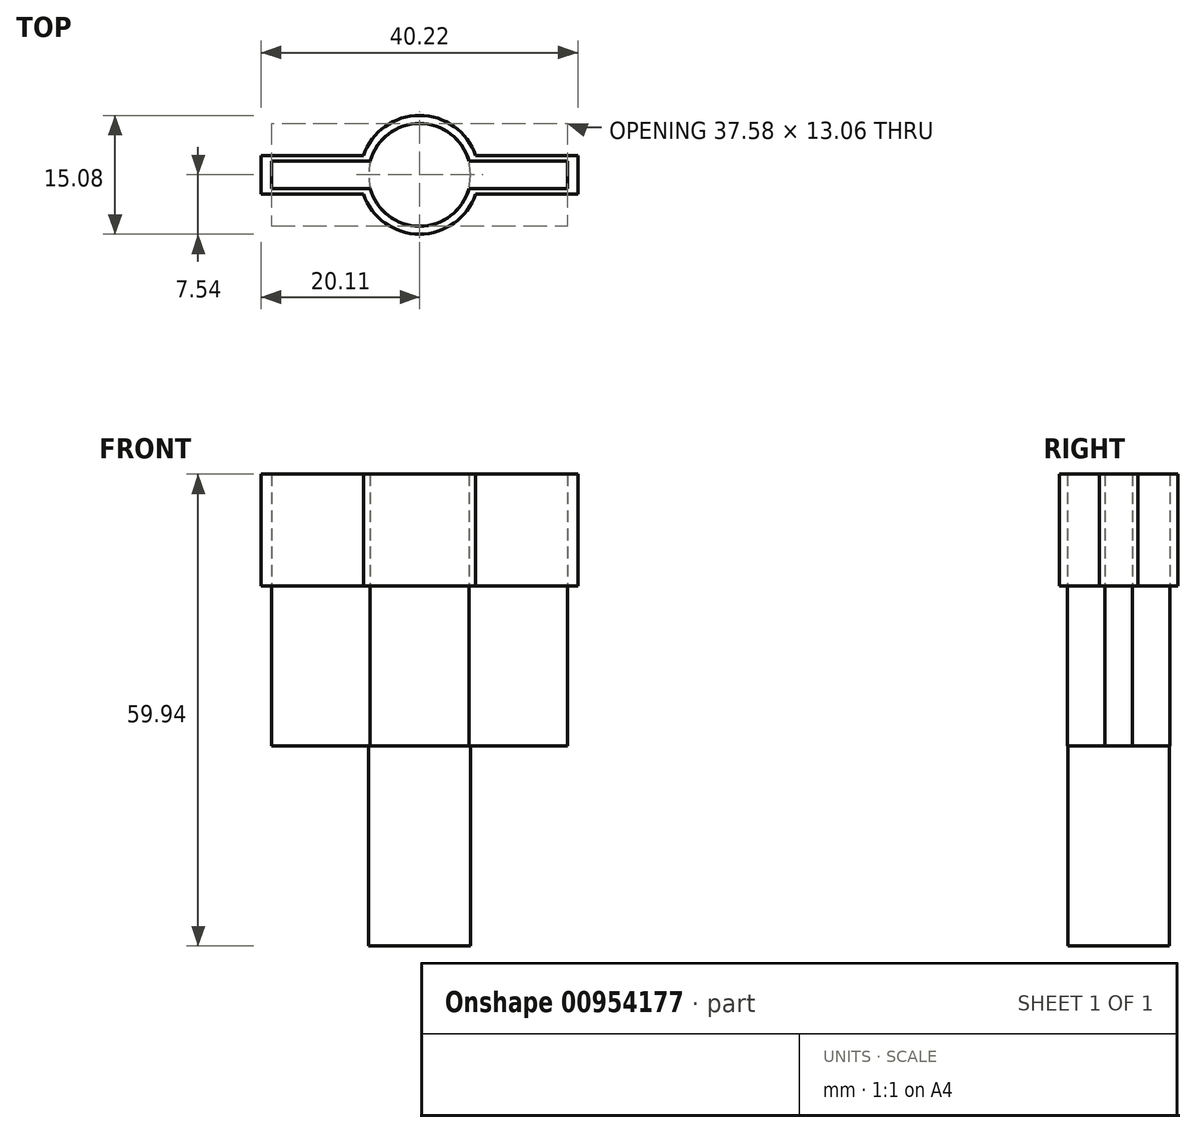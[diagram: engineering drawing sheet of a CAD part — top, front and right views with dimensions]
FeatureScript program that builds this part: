
annotation { "Feature Type Name" : "Feature", "Feature Type Description" : "" }
export const myFeature = defineFeature(function(context is Context, id is Id, definition is map)
    precondition{}
    {
        {
            var Q0;
            Q0=qCreatedBy(makeId("Top.planeOp"),FACE);
            var sketch = newSketch(context, id + "F0", { "sketchPlane" : qUnion([Q0])});
            skCircle(sketch, "E0", {"center": v(0, 0) * mm, "radius": 6.47 * mm});
            skSolve(sketch);
        }
        {
            var Q0;
            Q0=makeQuery(id+"F0.imprint","IMPRINT",FACE,{"disambiguationData":[TD([[makeQuery(id+"F0.imprint","IMPRINT",EDGE,{"derivedFrom":sQuery(id+"F0.wireOp",EDGE,"E0")}),1.0]])]});
            extrude(context, id + "F1", {"entities" : qUnion([Q0]), "depth" : 25.4 * mm, "offsetDistance" : 25.4 * mm});
        }
        {
            var Q0;
            Q0=makeQuery(id+"F1.opExtrude","CAP_FACE",FACE,{"disambiguationData":[OSD([sQuery(id+"F0.wireOp",EDGE,"E0")])],"isStart":false});
            var sketch = newSketch(context, id + "F2", { "sketchPlane" : qUnion([Q0])});
            skLineSegment(sketch, "E1.bottom", {"start": v(18.8, -1.74) * mm, "end": v(-18.8, -1.74) * mm});
            skLineSegment(sketch, "E1.top", {"start": v(18.8, 1.74) * mm, "end": v(-18.8, 1.74) * mm});
            skLineSegment(sketch, "E1.left", {"start": v(18.8, -1.74) * mm, "end": v(18.8, 1.74) * mm});
            skLineSegment(sketch, "E1.right", {"start": v(-18.8, -1.74) * mm, "end": v(-18.8, 1.74) * mm});
            skPoint(sketch, "E1.middle", {"position": v(0, 0) * mm});
            skCircle(sketch, "E2", {"center": v(0, 0) * mm, "radius": 6.52 * mm});
            skSolve(sketch);
        }
        {
            var Q0;
            Q0 = qSketchRegion(id + "F2", true);
            extrude(context, id + "F3", {"entities" : qUnion([Q0]), "operationType" : NewBodyOperationType.ADD, "depth" : 20.32 * mm, "offsetDistance" : 25.4 * mm});
        }
        {
            var Q0;
            Q0=makeQuery(id+"F3.opExtrude","CAP_FACE",FACE,{"disambiguationData":[OSD([sQuery(id+"F2.wireOp",EDGE,"E1.bottom"),sQuery(id+"F2.wireOp",EDGE,"E1.top"),sQuery(id+"F2.wireOp",EDGE,"E1.left"),sQuery(id+"F2.wireOp",EDGE,"E1.right"),sQuery(id+"F2.wireOp",EDGE,"E2")])],"isStart":false});
            var sketch = newSketch(context, id + "F4", { "sketchPlane" : qUnion([Q0])});
            skCircle(sketch, "E3", {"center": v(0, 0) * mm, "radius": 6.53 * mm});
            skLineSegment(sketch, "E4.bottom", {"start": v(18.8, -1.74) * mm, "end": v(6.3, -1.74) * mm});
            skLineSegment(sketch, "E4.top", {"start": v(18.8, 1.74) * mm, "end": v(6.3, 1.74) * mm});
            skLineSegment(sketch, "E4.left", {"start": v(18.8, -1.74) * mm, "end": v(18.8, 1.74) * mm});
            skLineSegment(sketch, "E4.right", {"start": v(-18.8, -1.74) * mm, "end": v(-18.8, 1.74) * mm});
            skArc(sketch, "E5", {"start": v(-7.13, -2.46) * mm, "mid": v(0, -7.54) * mm, "end": v(7.13, -2.46) * mm});
            skLineSegment(sketch, "E6.bottom", {"start": v(20.1, -2.46) * mm, "end": v(7.13, -2.46) * mm});
            skLineSegment(sketch, "E6.top", {"start": v(20.1, 2.46) * mm, "end": v(7.13, 2.46) * mm});
            skLineSegment(sketch, "E6.left", {"start": v(20.1, -2.46) * mm, "end": v(20.1, 2.46) * mm});
            skLineSegment(sketch, "E6.right", {"start": v(-20.1, -2.46) * mm, "end": v(-20.1, 2.46) * mm});
            skLineSegment(sketch, "E7.trimOffspring", {"start": v(-7.13, 2.46) * mm, "end": v(-20.1, 2.46) * mm});
            skLineSegment(sketch, "E8.trimOffspring", {"start": v(-7.13, -2.46) * mm, "end": v(-20.1, -2.46) * mm});
            skArc(sketch, "E9.trimOffspring", {"start": v(7.13, 2.46) * mm, "mid": v(0, 7.54) * mm, "end": v(-7.13, 2.46) * mm});
            skLineSegment(sketch, "E10.trimOffspring", {"start": v(-6.3, 1.74) * mm, "end": v(-18.8, 1.74) * mm});
            skLineSegment(sketch, "E11.trimOffspring", {"start": v(-6.3, -1.74) * mm, "end": v(-18.8, -1.74) * mm});
            skSolve(sketch);
        }
        {
            var Q0;
            Q0 = qSketchRegion(id + "F4", true);
            extrude(context, id + "F5", {"entities" : qUnion([Q0]), "depth" : 14.22 * mm, "offsetDistance" : 25.4 * mm});
        }
    });
